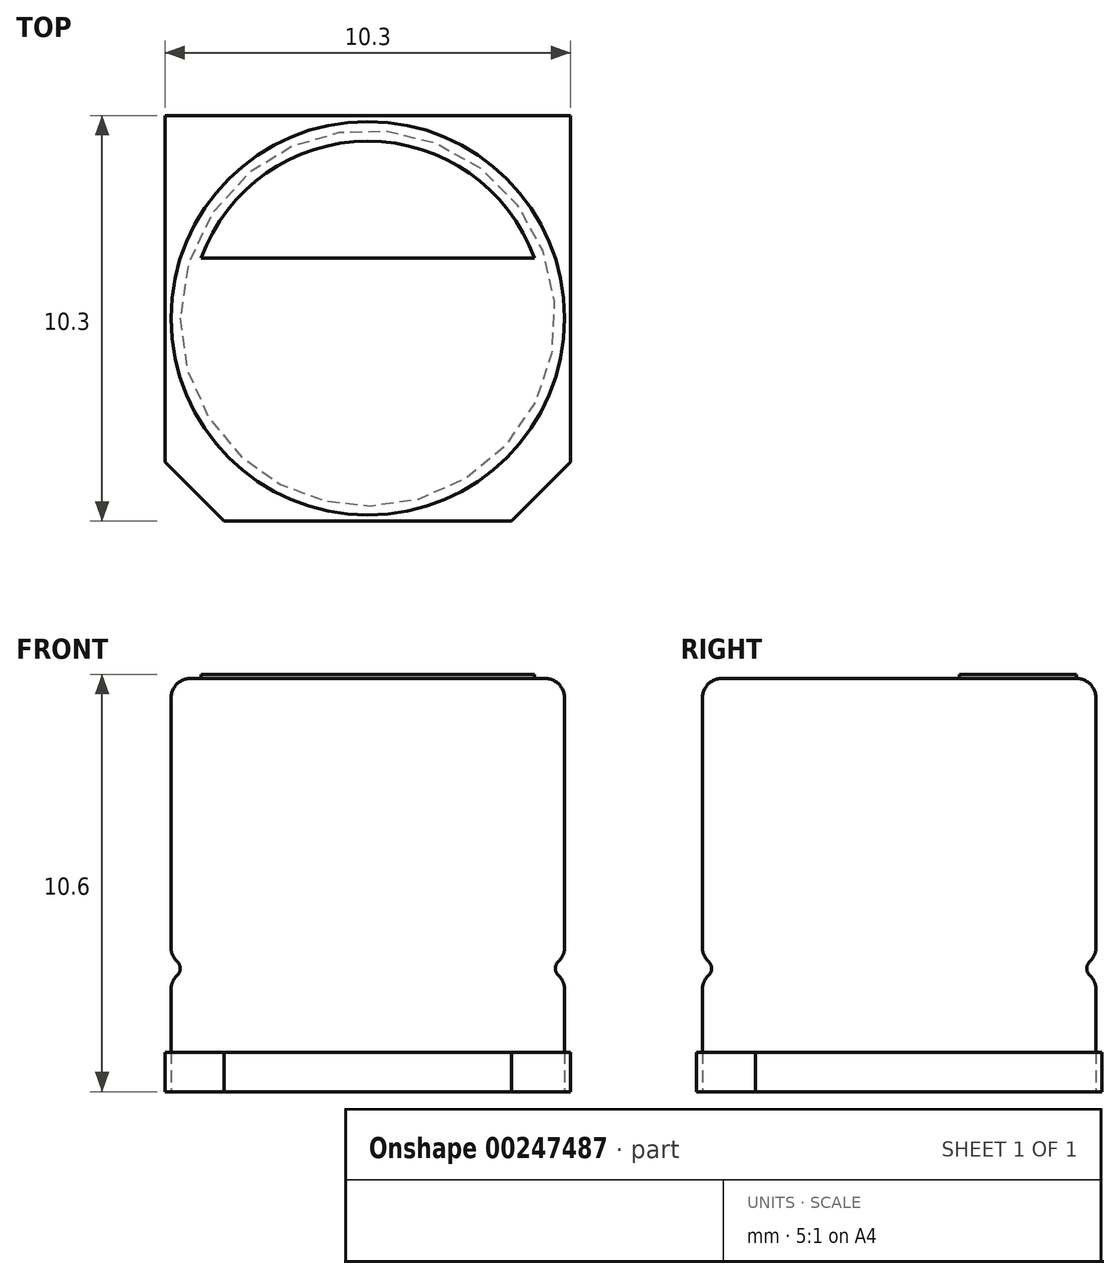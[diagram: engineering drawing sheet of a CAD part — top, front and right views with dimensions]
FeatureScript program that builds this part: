
annotation { "Feature Type Name" : "Feature", "Feature Type Description" : "" }
export const myFeature = defineFeature(function(context is Context, id is Id, definition is map)
    precondition{}
    {
        {
            var Q0;
            Q0=qCreatedBy(makeId("Front.planeOp"),FACE);
            var sketch = newSketch(context, id + "F0", { "sketchPlane" : qUnion([Q0])});
            skLineSegment(sketch, "E0.bottom", {"start": v(0, 0) * mm, "end": v(5, 0) * mm});
            skLineSegment(sketch, "E0.top", {"start": v(0, 10.5) * mm, "end": v(5, 10.5) * mm});
            skLineSegment(sketch, "E0.left", {"start": v(0, 0) * mm, "end": v(0, 10.5) * mm});
            skLineSegment(sketch, "E0.right", {"start": v(5, 0) * mm, "end": v(5, 2.9) * mm});
            skArc(sketch, "E1", {"start": v(5, 3.37) * mm, "mid": v(4.77, 3.13) * mm, "end": v(5, 2.9) * mm});
            skLineSegment(sketch, "E2.trimOffspring", {"start": v(5, 3.37) * mm, "end": v(5, 10.5) * mm});
            skSolve(sketch);
        }
        {
            var Q0;
            Q0=makeQuery(id+"F0.imprint","IMPRINT",FACE,{"disambiguationData":[TD([[makeQuery(id+"F0.imprint","IMPRINT",EDGE,{"derivedFrom":sQuery(id+"F0.wireOp",EDGE,"E0.bottom")}),1.0]])]});
            var Q1;
            Q1=sQuery(id+"F0.wireOp",EDGE,"E0.left");
            revolve(context, id + "F1", {"entities" : qUnion([Q0]), "axis" : qUnion([Q1]), "revolveType" : RevolveType.FULL});
        }
        {
            var Q0;
            Q0=makeQuery(id+"F1.opRevolve","SWEPT_EDGE",EDGE,{"disambiguationData":[OSD([sQuery(id+"F0.wireOp",EDGE,"E0.top"),sQuery(id+"F0.wireOp",EDGE,"E2.trimOffspring")])]});
            var Q1;
            Q1=makeQuery(id+"F1.opRevolve","SWEPT_EDGE",EDGE,{"disambiguationData":[OSD([sQuery(id+"F0.wireOp",EDGE,"E1"),sQuery(id+"F0.wireOp",EDGE,"E2.trimOffspring")])]});
            var Q2;
            Q2=makeQuery(id+"F1.opRevolve","SWEPT_EDGE",EDGE,{"disambiguationData":[OSD([sQuery(id+"F0.wireOp",EDGE,"E0.right"),sQuery(id+"F0.wireOp",EDGE,"E1")])]});
            fillet(context, id + "F2", {"entities" : qUnion([Q0, Q1, Q2]), "radius" : .5 * mm, "tangentPropagation" : true, "allowEdgeOverflow" : false});
        }
        {
            var Q0;
            Q0=makeQuery(id+"F1.opRevolve","SWEPT_FACE",FACE,{"disambiguationData":[OSD([sQuery(id+"F0.wireOp",EDGE,"E0.bottom")])]});
            var sketch = newSketch(context, id + "F3", { "sketchPlane" : qUnion([Q0])});
            skLineSegment(sketch, "E3.rect.bottom", {"start": v(5.15, -5.15) * mm, "end": v(-5.15, -5.15) * mm});
            skLineSegment(sketch, "E3.rect.top", {"start": v(5.15, 5.15) * mm, "end": v(-5.15, 5.15) * mm});
            skLineSegment(sketch, "E3.rect.left", {"start": v(5.15, -5.15) * mm, "end": v(5.15, 5.15) * mm});
            skLineSegment(sketch, "E3.rect.right", {"start": v(-5.15, -5.15) * mm, "end": v(-5.15, 5.15) * mm});
            skPoint(sketch, "E3.rect.middle", {"position": v(0, 0) * mm});
            skSolve(sketch);
        }
        {
            var Q0;
            Q0=qSketchRegion(id+"F3",true);
            extrude(context, id + "F4", {"entities" : qUnion([Q0]), "oppositeDirection" : true, "depth" : 1 * mm});
        }
        {
            var Q0;
            Q0=makeQuery(id+"F4.opExtrude","SWEPT_EDGE",EDGE,{"disambiguationData":[OSD([sQuery(id+"F3.wireOp",EDGE,"E3.rect.top"),sQuery(id+"F3.wireOp",EDGE,"E3.rect.right")])]});
            var Q1;
            Q1=makeQuery(id+"F4.opExtrude","SWEPT_EDGE",EDGE,{"disambiguationData":[OSD([sQuery(id+"F3.wireOp",EDGE,"E3.rect.top"),sQuery(id+"F3.wireOp",EDGE,"E3.rect.left")])]});
            chamfer(context, id + "F5", {"entities" : qUnion([Q0, Q1]), "width" : 1.5 * mm, "tangentPropagation" : true});
        }
        {
            var Q0;
            Q0=makeQuery(id+"F1.opRevolve","SWEPT_FACE",FACE,{"disambiguationData":[OSD([sQuery(id+"F0.wireOp",EDGE,"E0.top")])]});
            var sketch = newSketch(context, id + "F6", { "sketchPlane" : qUnion([Q0])});
            skLineSegment(sketch, "E4.top", {"start": v(-4.23, 1.53) * mm, "end": v(4.23, 1.53) * mm});
            skArc(sketch, "E5", {"start": v(-4.23, 1.53) * mm, "mid": v(0, 4.5) * mm, "end": v(4.23, 1.53) * mm});
            skSolve(sketch);
        }
        {
            var Q0;
            Q0=qSketchRegion(id+"F6",true);
            extrude(context, id + "F7", {"entities" : qUnion([Q0]), "depth" : .1 * mm});
        }
    });
